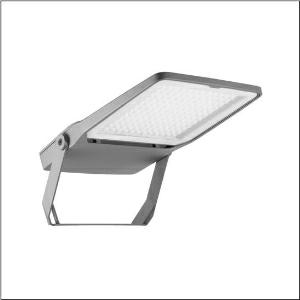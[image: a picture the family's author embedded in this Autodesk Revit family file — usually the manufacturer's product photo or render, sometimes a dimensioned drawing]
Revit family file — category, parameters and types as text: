
# Revit family: floodlight_fl_20_midi___rs17_5xa7682e2b1ac_5cc3
name_source: partatom
category: Lighting Fixtures
units: mm (PartAtom-declared; Revit-internal decimal feet)

## family parameters
Cut with Voids When Loaded = No
Host = Face
Light Source = No
Part Type = Normal
Room Calculation Point = No
Round Connector Dimension = Use Diameter
Shared = No

## types (1)
- --- (1 x LED 4000K / CRI = 70 (unbekannt), 29150 lm, 4000K)
    Apparent Load = 208 VA
    CIE Flux Codes = 79 92 99 100 100
    Color Rendering = 70
    Color Temperature = 4000K
    Default Elevation = 1800 mm
    Description = Floodlight FL 20 midi, floodlight, primary light control with lens, of plastic, primary optical cover: protective disc, of toughened safety glass, transparent, light distribution: RS17, light emission: direct distribution, primary light characteristic: rotationally symmetric, installation type: surface-mounted, LED, High Power LED, rated luminous flux: 29.150lm, luminous efficacy: 140lm/W, light colour: 740, colour temperature: 4000K, control gear: ECG Plus, control: flexible luminous flux parameterisation, time-dependent luminous flux control, digital communication interface, power reduction, overheat protection, electronic power reduction, with terminal, 5-pole, max. 2.5mm², mains connection: 220..240V, AC, 50/60Hz, rated input power: 208W, LED unit, of diecast aluminium, powder-coated, Siteco® metallic grey (DB 702S), corrosivity category C5 mid according to DIN EN ISO 12944, incl. 1x M20 cable gland for cable Ø 6.5..12mm, length: 654mm, width: 450mm, height: 76mm, housing frame, of diecast aluminium, powder-coated, Siteco® metallic grey (DB 702S), mounting bracket, of steel, powder-coated, Siteco® metallic grey (DB 702S), DALI, protection rating (complete): IP66, insulation class (complete): insulation class II (safety insulation), certification: CE, ENEC, VDE, protection symbol: D, permissible operating ambient temperature: -40..+40°C, permissible operating ambient temperature for outdoor applications: -40..+50°C, standard: DIN EN 12944, packaging unit: 1 piece

Light Distribution: RS17
    Height = 76 mm
    Lamp = 1 x LED 4000K / CRI >= 70 (unbekannt)
    Lamp Light Flux = 29150 lm
    Lamp count = 1
    Length = 672 mm
    Luminous efficacy = 140 lm/W
    Manufacturer = Siteco
    ModVariant = No
    Model = 5XA7682E2B1AC
    Mounting Place = Wall
    Mounting Type = Surface mounted
    Number of Poles = 1
    OnlyDefault = Yes
    Power Factor = 1
    Product Name = Floodlight FL 20 midi | RS17
    Product group = floodlight | wall mounted
    ProductGroupID = 2001
    Protection Class = Protection class II
    Protection Degree = IP 66
    RLX_Detail_Level = 1
    RLX_Emergency_Light_Flux = 0 lm
    RLX_Emergency_Type = 0
    RLX_Emergency_Type_DB = No
    RlxData = <blob elided: 92433 chars, md5=0595f669>
    Socket = socket
    Standby Power = 0 W
    System Light Flux = 29150 lm
    System Power = 208 W
    Type Comments = factory setting: luminous flux: 100 % | dim-lin: 254 | 484 mA
    Type Image = l_1005943.jpg
    URL = http://relux.com
    VarID = @adj_146449
    Voltage = 0 V
    Weight = 0.00 kg
    Width = 450 mm

## geometry (parser evidence)
native form markers: Blend x4, Sweep x13
no freeform markers — native parametric forms only
